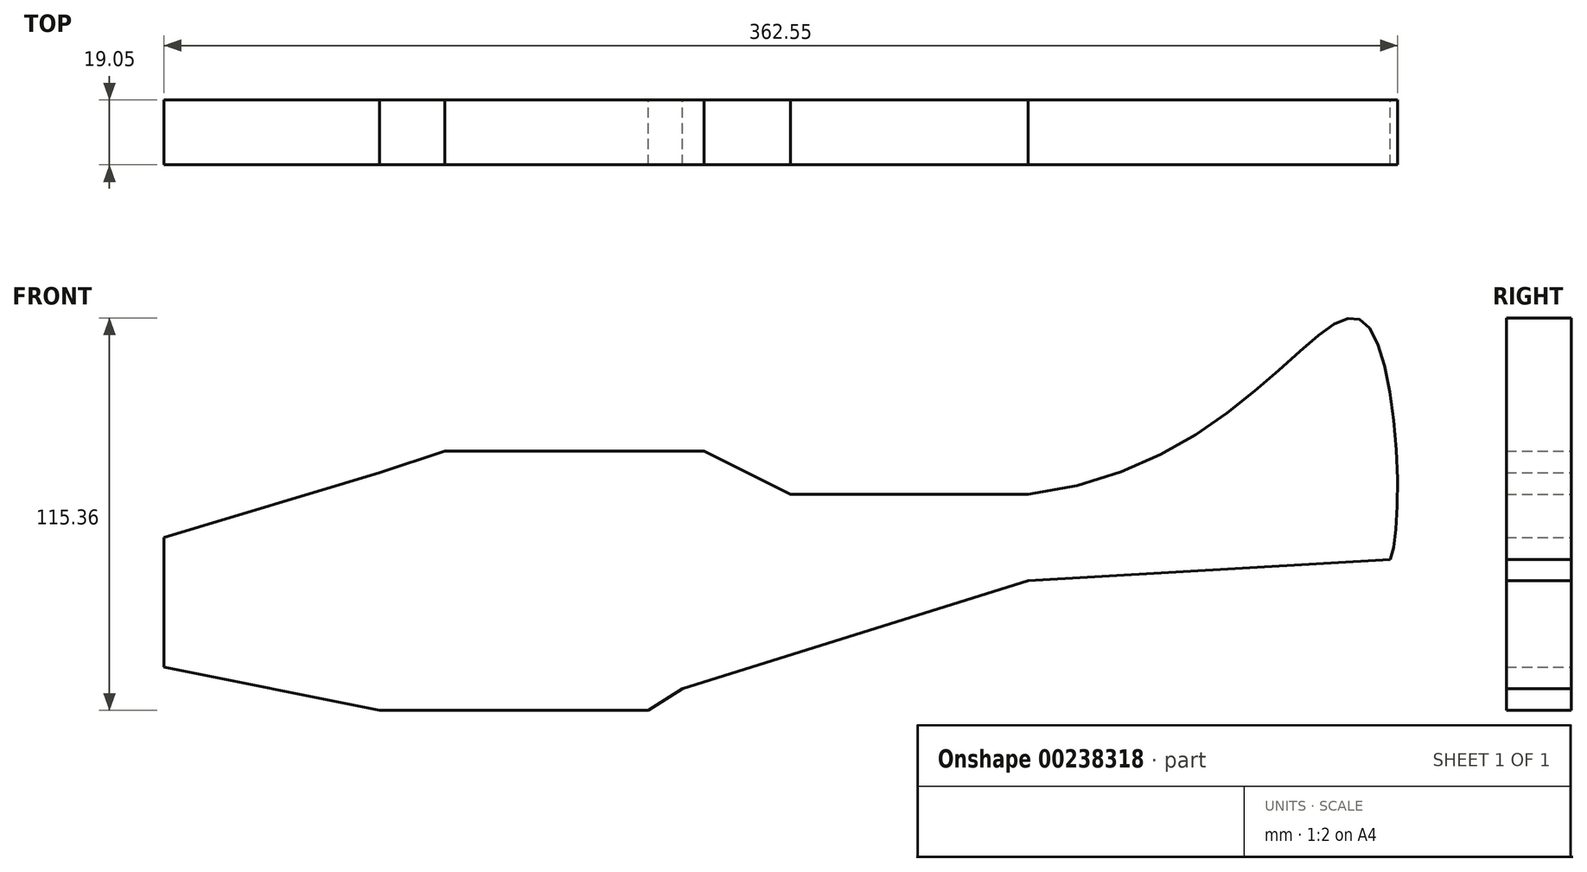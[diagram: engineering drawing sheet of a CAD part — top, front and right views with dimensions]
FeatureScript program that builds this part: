
annotation { "Feature Type Name" : "Feature", "Feature Type Description" : "" }
export const myFeature = defineFeature(function(context is Context, id is Id, definition is map)
    precondition{}
    {
        {
            var Q0;
            Q0=qCreatedBy(makeId("Front.planeOp"),FACE);
            var sketch = newSketch(context, id + "F0", { "sketchPlane" : qUnion([Q0])});
            skLineSegment(sketch, "E0", {"start": v(-180.97, -47.63) * mm, "end": v(-180.97, -9.53) * mm});
            skLineSegment(sketch, "E1", {"start": v(-117.65, 9.52) * mm, "end": v(-180.97, -9.53) * mm});
            skLineSegment(sketch, "E2", {"start": v(-117.65, 9.52) * mm, "end": v(-98.42, 15.87) * mm});
            skLineSegment(sketch, "E3", {"start": v(-180.97, -47.63) * mm, "end": v(-117.65, -60.33) * mm});
            skLineSegment(sketch, "E4", {"start": v(-22.23, 15.87) * mm, "end": v(-98.42, 15.87) * mm});
            skLineSegment(sketch, "E5", {"start": v(3.18, 3.17) * mm, "end": v(-22.22, 15.88) * mm});
            skLineSegment(sketch, "E6", {"start": v(73.03, 3.17) * mm, "end": v(3.18, 3.17) * mm});
            skLineSegment(sketch, "E7", {"start": v(73.03, -22.23) * mm, "end": v(180.98, -15.88) * mm});
            skFitSpline(sketch, "E8", {"points": [v(73.03, 3.17) * mm, v(171.45, 53.97) * mm, v(180.46, -12.13) * mm, v(176.18, -20.19) * mm], "startDerivative": vector(383.27, 42.8) * mm, "endDerivative": vector(-33.07, -31.63) * mm});
            skLineSegment(sketch, "E9", {"start": v(73.03, -22.23) * mm, "end": v(-28.58, -53.98) * mm});
            skLineSegment(sketch, "E10", {"start": v(-28.58, -53.98) * mm, "end": v(-38.64, -60.33) * mm});
            skLineSegment(sketch, "E11", {"start": v(-117.65, -60.33) * mm, "end": v(-38.64, -60.33) * mm});
            skSolve(sketch);
        }
        {
            var Q0;
            Q0 = qSketchRegion(id + "F0", true);
            extrude(context, id + "F1", {"entities" : qUnion([Q0]), "depth" : 19.05 * mm});
        }
    });
